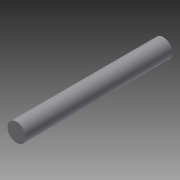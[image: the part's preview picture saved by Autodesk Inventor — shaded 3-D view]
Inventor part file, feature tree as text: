
AUTODESK INVENTOR PART (.ipt)
format: ipt  version: 2013 (Build 170138000, 138)  size: 69,632 bytes
history: native  units: in
note: dims shown in document units (in); Inventor stores cm internally (conversion verified against a paired STEP export)
features: extrude x1, sketch x1
ambient origin geometry x8: Origin, YZ Plane, XZ Plane, XY Plane, X Axis, Y Axis, Z Axis, Center Point
bodies: Solid1 (feature_tree)
feature tree (2):
  extrude  "Extrusion1"  Depth=1.5in TaperAngle=0.0deg
  sketch  "Sketch1"  dims[d0=0.1875in d3=1.5in d4=0.0in]
